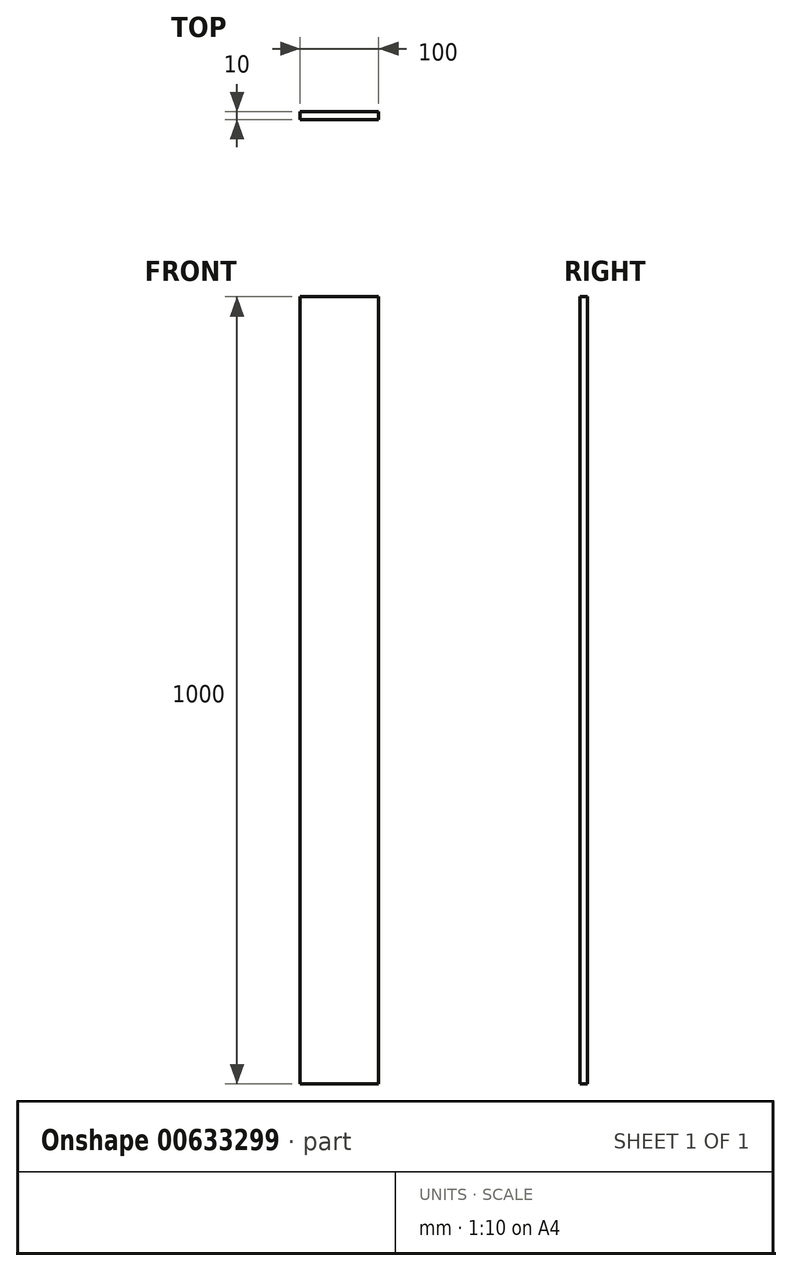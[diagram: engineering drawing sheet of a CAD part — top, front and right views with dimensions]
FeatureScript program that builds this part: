
annotation { "Feature Type Name" : "Feature", "Feature Type Description" : "" }
export const myFeature = defineFeature(function(context is Context, id is Id, definition is map)
    precondition{}
    {
        {
            var Q0;
            Q0=qCreatedBy(makeId("Front.planeOp"),FACE);
            var sketch = newSketch(context, id + "F0", { "sketchPlane" : qUnion([Q0])});
            skLineSegment(sketch, "E0.bottom", {"start": v(50, 500) * mm, "end": v(-50, 500) * mm});
            skLineSegment(sketch, "E0.top", {"start": v(50, -500) * mm, "end": v(-50, -500) * mm});
            skLineSegment(sketch, "E0.left", {"start": v(50, 500) * mm, "end": v(50, -500) * mm});
            skLineSegment(sketch, "E0.right", {"start": v(-50, 500) * mm, "end": v(-50, -500) * mm});
            skPoint(sketch, "E0.middle", {"position": v(0, 0) * mm});
            skSolve(sketch);
        }
        {
            var Q0;
            Q0 = qSketchRegion(id + "F0", true);
            extrude(context, id + "F1", {"entities" : qUnion([Q0]), "endBound" : BoundingType.SYMMETRIC, "depth" : 10 * mm, "offsetDistance" : 25 * mm});
        }
    });
